# Revit family: PRE080026-FR
name_source: partatom
category: Appareils sanitaires
revit_build: Autodesk Revit 2017 (Build: 20160225_1515(x64)
units: mm (PartAtom-declared; Revit-internal decimal feet)

## family parameters
Basée sur le plan de construction = Non
Cote de connecteur circulaire = Utiliser le diamètre
Couper avec des vides une fois chargée = Non
Partagée = Non
Point de calcul de pièce = Non
Toujours verticalement = Oui
Type d'élément = Normal

## types (1)
- 70828 PRESTO CHEF Colonne deux trous sur plage avec douchette et bec de remplissage
    Adresse = 7, RUE RACINE - 92542 MONTROUGE CEDEX FRANCE
    Debit = 1,9l/min avec limiteur de débit intégré
 (sprayer)
 Dispositif anti-coup de bélier

 Brise-jet : anti-vandalisme et anti-bouchage
    Description = Produit résistant à un usage intensif
Souplesse du ressort
Douchette ergonomique avec fonction écoulement continu, et surface de préhension limitant les risques de brûlure. Embout permettant d'absorber les chocs
Remplissage rapide de cuves : 30L/min à 3 bar
Interface corps/colonne renforcé
Volants intuitifs et ergonomiques : facilité de préhension
Support mural réglable
Crochet de blocage pour éviter les TMS (trouble musculo squeletiques)
Flexible de douchette gaine PVC pour éviter les niches bactériennes et faciliter le nettoyage
Maintenance aisée : présence d'une fente sous la pastile rouge/bleue permettant le passage d'un tournevis
Facilité de maintenance : disponibilité de toutes les pièces d'usure
Brise-jet pour canaliser l'eau et éviter les projections d'eau latérales
    Diamètre Nominal = 15 mm  [stored 0.0492126 ft]
    Edition number = 0
    Fabricant = LES ROBINETS PRESTO S.A.
    Finition = Corps en laiton chromé conforme aux normes NF EN1982/ NF EN 12164 / NF EN 12165
Traitement de surface Nickel-Chrome selon NF EN12540
Résistance au brouillard salin neutre (NSS) : 200 h selon NF ISO 9240
    Flux = 0.0 L/s
    Fonction = Robinet tête céramique 1/4 de tour avec bec de remplissage Lg 300 mm - orientable
Douchette noire M 1/2'' avec surface de préhension limitant les risques de brûlures
Débit de douchette : 12L/Min (régulé) - Jet réglable par l'utilisateur : concentré ou mouillage - Embout de douchette anti-tartre - Crochet de blocage pour écoulement
continu - clapet anti-retour NF intégré
Brise-jet anti-tartre interchangeable
Ressort de guidage pour flexible en inox
Support mural réglable, recoupable de 60 à 200 mm (de la colonne au mur)
Support de douchette ajustable à gauche ou à droite

Pression d'utilisation recommandée : 1 à 5 bars

Débit : 30L/min à 3 bar

Alimentation hydraulique : G 1/2'' (15x 21)

Matière et couleur de finition :
Corps, bec et colonne en laiton chromé
Matière conforme avec la liste "UBA"

Résistance thermique : Résiste à une température de 75° C durant 30 minutes (dans le cadre de chocs thermiques).

Livré avec :
Colonnettes avec écrou
2 filtres
1 flexible (de douchette) tressé inox entouré d'une gaine PVC, résistant à des températures allant jusqu'à 90°C. Température d'utilisation en service à 70°C maximum
en continu
    Hauteur = 1171 mm  [stored 3.84186 ft]
    LC = 15 mm  [stored 0.0492126 ft]
    Largeur = 215 mm  [stored 0.705381 ft]
    Lien CCTP = http://www.prestodatashare.com
    Lien fiche produit = http://www.prestodatashare.com
    Lien notice d'utilisation = http://www.prestodatashare.com
    Matériau = Laiton poli chromé
    Modèle = 70828 PRESTO CHEF Colonne deux trous sur plage avec douchette et bec de remplissage
    PC = 150 mm  [stored 0.492126 ft]
    Perte de charge = 0.0 Pa
    Polantis code = PRE080026
    Product Guid = 75823008-ad45-4655-8c87-8420e3ee1b5c
    Product data url = https://www.bimobject.com
    Profondeur = 543 mm  [stored 1.7815 ft]
    Raccordement = 2xG1/2 entraxe 150 dessous milieu
    Reference = 70828
    URL = http://www.prestodatashare.com
    URL Fabricant = http://www.prestodatashare.com
    Variantes = 70828

note: [stored X ft] marks values corroborated as IEEE doubles in the binary element streams (Revit-internal decimal feet)
